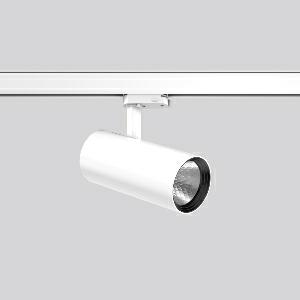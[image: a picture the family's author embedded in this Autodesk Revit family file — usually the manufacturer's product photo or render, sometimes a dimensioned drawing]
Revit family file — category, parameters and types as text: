
# Revit family: deecos_s_mini_742203_002_3_f597
name_source: partatom
category: Lighting Fixtures
units: mm (PartAtom-declared; Revit-internal decimal feet)

## family parameters
Cut with Voids When Loaded = No
Host = Face
Light Source = No
Part Type = Normal
Room Calculation Point = No
Round Connector Dimension = Use Diameter
Shared = No

## types (1)
- DEECOS S mini (1 x LED Modul 935, 3700 lm, 3500)
    Apparent Load = 29 VA
    Approval mark = CE
    CIE Flux Codes = 100 100 100 100 100
    Color Rendering = 92
    Color Temperature = 3500
    Default Elevation = 1800 mm
    Description = Series: DEECOS S mini
LED surface-mounted projector in modern design with no visible cooling ribs. Housing: die-cast aluminium, powder-coated. Rotation range: 356°. Swivel range: 90°. Black plastic ring and recessed LED to prevent glare from the side. Optical assembly with reflector made of MIRO-Silver with 98% total light reflection for outstanding efficiency - can be changed without tools. Best colour rendering index Ra>90. With multi adaptor for 3-circuit tracks 230 V. Suitable for Track on ceiling, Wall track. High quality converter without flickering and stroboscopic effect. The following accessories can be mounted without use of tools: interchangeable lenses, decorative glasses, honeycomb louvre, clear and frosted diffusers, white interchangeable plastic ring. 
Colour: traffic white, matt (RAL 9016)
Diameter: 87 mm
Height: 214 mm
Lamp: LED
Socket: without socket
Colour temperature: 3500K
Colour rendering index (CRI): 92
System power: 29 W
Rated luminous flux: 3700 lm
Luminous efficiency: 128 lm/W
Control gear: Regulated power supply
Protection class: I
Type of protection: IP 20
    Height = 214 mm
    Lamp = 1 x LED Modul 935
    Lamp Light Flux = 3700 lm
    Lamp count = 1
    Length = 87 mm
    Lifetime = 50000 h
    Luminous efficacy = 128 lm/W
    Manufacturer = RZB
    ModVariant = No
    Model = 742203.002.3
    Mounting Place = Ceiling
    Mounting Type = Rail mounted
    Number of Poles = 1
    OnlyDefault = Yes
    Power Factor = 1
    Product Name = DEECOS S mini
    Product group = Track mounted projectors
    ProductGroupID = 301
    Protection Class = Protection class I
    Protection Degree = IP 20
    RLX_Detail_Level = 1
    RLX_Emergency_Light_Flux = 0 lm
    RLX_Emergency_Type = 0
    RLX_Emergency_Type_DB = No
    RlxData = <blob elided: 34965 chars, md5=c1161a2d>
    Socket = socket
    Standby Power = 0 W
    System Light Flux = 3700 lm
    System Power = 29 W
    Type Comments = Product without accessories
    Type Image = 741926.002.jpg
    URL = http://relux.com
    VarID = ---
    Voltage = 230 V
    Voltage Range = 220-240 V
    Weight = 0.00 kg
    Width = 0 mm  [stored 0 ft]

note: [stored X ft] marks values corroborated as IEEE doubles in the binary element streams (Revit-internal decimal feet)

## geometry (parser evidence)
native form markers: Blend x4, Sweep x12
no freeform markers — native parametric forms only
